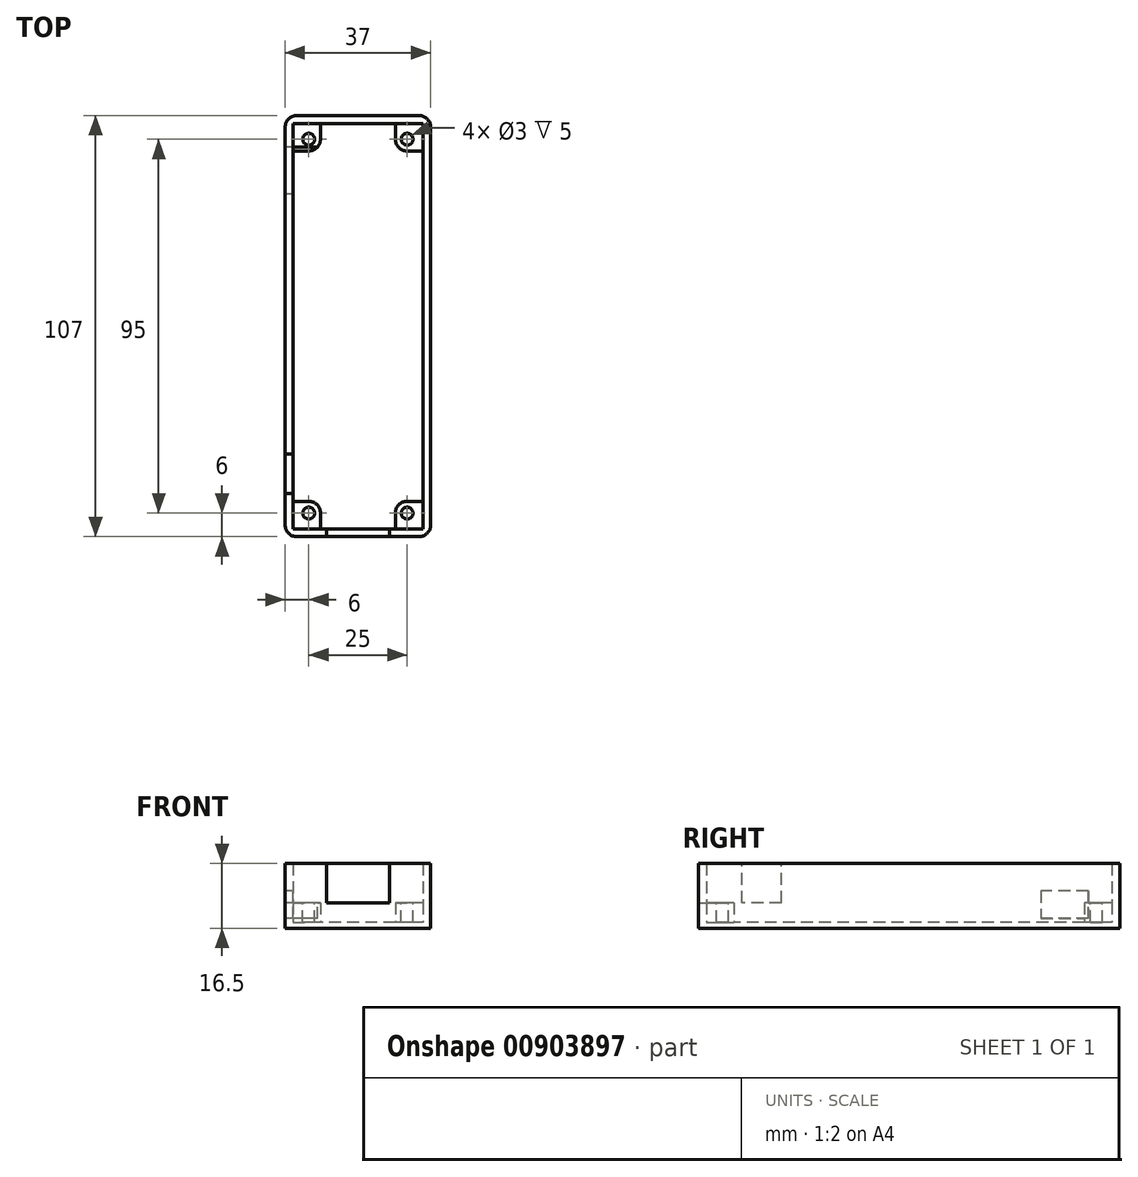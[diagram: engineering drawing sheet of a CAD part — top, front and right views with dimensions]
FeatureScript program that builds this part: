
annotation { "Feature Type Name" : "Feature", "Feature Type Description" : "" }
export const myFeature = defineFeature(function(context is Context, id is Id, definition is map)
    precondition{}
    {
        {
            var Q0;
            Q0=qCreatedBy(makeId("Top.planeOp"),FACE);
            var sketch = newSketch(context, id + "F0", { "sketchPlane" : qUnion([Q0])});
            skLineSegment(sketch, "E0.bottom", {"start": v(18.5, 53.5) * mm, "end": v(-18.5, 53.5) * mm});
            skLineSegment(sketch, "E0.top", {"start": v(18.5, -53.5) * mm, "end": v(-18.5, -53.5) * mm});
            skLineSegment(sketch, "E0.left", {"start": v(18.5, 53.5) * mm, "end": v(18.5, -53.5) * mm});
            skLineSegment(sketch, "E0.right", {"start": v(-18.5, 53.5) * mm, "end": v(-18.5, -53.5) * mm});
            skPoint(sketch, "E0.middle", {"position": v(0, 0) * mm});
            skSolve(sketch);
        }
        {
            var Q0;
            Q0=makeQuery(id+"F0.imprint","IMPRINT",FACE,{"disambiguationData":[TD([[makeQuery(id+"F0.imprint","IMPRINT",EDGE,{"derivedFrom":sQuery(id+"F0.wireOp",EDGE,"E0.bottom")}),1.0]])]});
            extrude(context, id + "F1", {"entities" : qUnion([Q0]), "depth" : 1.5 * mm, "offsetDistance" : 25 * mm});
        }
        {
            var Q0;
            Q0=makeQuery(id+"F1.opExtrude","CAP_FACE",FACE,{"disambiguationData":[OSD([sQuery(id+"F0.wireOp",EDGE,"E0.bottom"),sQuery(id+"F0.wireOp",EDGE,"E0.top"),sQuery(id+"F0.wireOp",EDGE,"E0.left"),sQuery(id+"F0.wireOp",EDGE,"E0.right")])],"isStart":false});
            var sketch = newSketch(context, id + "F2", { "sketchPlane" : qUnion([Q0])});
            skLineSegment(sketch, "E1.bottom", {"start": v(16.5, 51.5) * mm, "end": v(-16.5, 51.5) * mm});
            skLineSegment(sketch, "E1.top", {"start": v(16.5, -51.5) * mm, "end": v(-16.5, -51.5) * mm});
            skLineSegment(sketch, "E1.left", {"start": v(16.5, 51.5) * mm, "end": v(16.5, -51.5) * mm});
            skLineSegment(sketch, "E1.right", {"start": v(-16.5, 51.5) * mm, "end": v(-16.5, -51.5) * mm});
            skPoint(sketch, "E1.middle", {"position": v(0, 0) * mm});
            skSolve(sketch);
        }
        {
            var Q0;
            Q0=makeQuery(id+"F2.imprint","IMPRINT",FACE,{"disambiguationData":[TD([[makeQuery(id+"F2.imprint","IMPRINT",EDGE,{"derivedFrom":sQuery(id+"F2.wireOp",EDGE,"E1.bottom")}),-1.0]])]});
            extrude(context, id + "F3", {"entities" : qUnion([Q0]), "operationType" : NewBodyOperationType.ADD, "depth" : 15 * mm, "offsetDistance" : 25 * mm});
        }
        {
            var Q0;
            Q0=makeQuery(id+"F1.opExtrude","CAP_FACE",FACE,{"disambiguationData":[OSD([sQuery(id+"F0.wireOp",EDGE,"E0.bottom"),sQuery(id+"F0.wireOp",EDGE,"E0.top"),sQuery(id+"F0.wireOp",EDGE,"E0.left"),sQuery(id+"F0.wireOp",EDGE,"E0.right")])],"isStart":false});
            var sketch = newSketch(context, id + "F4", { "sketchPlane" : qUnion([Q0])});
            skLineSegment(sketch, "E2.bottom", {"start": v(-16.5, 51.5) * mm, "end": v(-9.5, 51.5) * mm});
            skLineSegment(sketch, "E2.top", {"start": v(-16.5, 44.5) * mm, "end": v(-9.5, 44.5) * mm});
            skLineSegment(sketch, "E2.left", {"start": v(-16.5, 51.5) * mm, "end": v(-16.5, 44.5) * mm});
            skLineSegment(sketch, "E2.right", {"start": v(-9.5, 51.5) * mm, "end": v(-9.5, 44.5) * mm});
            skLineSegment(sketch, "E3.MirrorCS", {"start": v(16.5, 51.5) * mm, "end": v(9.5, 51.5) * mm});
            skLineSegment(sketch, "E4.MirrorCS", {"start": v(9.5, 51.5) * mm, "end": v(9.5, 44.5) * mm});
            skLineSegment(sketch, "E5.MirrorCS", {"start": v(16.5, 44.5) * mm, "end": v(9.5, 44.5) * mm});
            skLineSegment(sketch, "E6.MirrorCS", {"start": v(16.5, 51.5) * mm, "end": v(16.5, 44.5) * mm});
            skLineSegment(sketch, "E7.MirrorCS", {"start": v(16.5, -44.5) * mm, "end": v(9.5, -44.5) * mm});
            skLineSegment(sketch, "E8.MirrorCS", {"start": v(-9.5, -51.5) * mm, "end": v(-9.5, -44.5) * mm});
            skLineSegment(sketch, "E9.MirrorCS", {"start": v(-16.5, -51.5) * mm, "end": v(-9.5, -51.5) * mm});
            skLineSegment(sketch, "E10.MirrorCS", {"start": v(16.5, -51.5) * mm, "end": v(16.5, -44.5) * mm});
            skLineSegment(sketch, "E11.MirrorCS", {"start": v(-16.5, -44.5) * mm, "end": v(-9.5, -44.5) * mm});
            skLineSegment(sketch, "E12.MirrorCS", {"start": v(-16.5, -51.5) * mm, "end": v(-16.5, -44.5) * mm});
            skLineSegment(sketch, "E13.MirrorCS", {"start": v(9.5, -51.5) * mm, "end": v(9.5, -44.5) * mm});
            skLineSegment(sketch, "E14.MirrorCS", {"start": v(16.5, -51.5) * mm, "end": v(9.5, -51.5) * mm});
            skSolve(sketch);
        }
        {
            var Q0;
            Q0 = qSketchRegion(id + "F4", true);
            extrude(context, id + "F5", {"entities" : qUnion([Q0]), "operationType" : NewBodyOperationType.ADD, "depth" : 5 * mm, "offsetDistance" : 25 * mm});
        }
        {
            var Q0;
            Q0=makeQuery(id+"F5.opExtrude","CAP_FACE",FACE,{"disambiguationData":[OSD([sQuery(id+"F4.wireOp",EDGE,"E2.bottom"),sQuery(id+"F4.wireOp",EDGE,"E2.top"),sQuery(id+"F4.wireOp",EDGE,"E2.left"),sQuery(id+"F4.wireOp",EDGE,"E2.right")])],"isStart":false});
            var sketch = newSketch(context, id + "F6", { "sketchPlane" : qUnion([Q0])});
            skLineSegment(sketch, "E15.bottom", {"start": v(12.5, 47.5) * mm, "end": v(-12.5, 47.5) * mm, "construction": true});
            skLineSegment(sketch, "E15.top", {"start": v(12.5, -47.5) * mm, "end": v(-12.5, -47.5) * mm, "construction": true});
            skLineSegment(sketch, "E15.left", {"start": v(12.5, 47.5) * mm, "end": v(12.5, -47.5) * mm, "construction": true});
            skLineSegment(sketch, "E15.right", {"start": v(-12.5, 47.5) * mm, "end": v(-12.5, -47.5) * mm, "construction": true});
            skPoint(sketch, "E15.middle", {"position": v(0, 0) * mm});
            skCircle(sketch, "E16", {"center": v(-12.5, 47.5) * mm, "radius": 1.5 * mm});
            skCircle(sketch, "E17.MirrorC", {"center": v(12.5, 47.5) * mm, "radius": 1.5 * mm});
            skLineSegment(sketch, "E18.MirrorCS", {"start": v(-12.5, 47.5) * mm, "end": v(12.5, 47.5) * mm, "construction": true});
            skLineSegment(sketch, "E19.MirrorCS", {"start": v(-12.5, -47.5) * mm, "end": v(12.5, -47.5) * mm, "construction": true});
            skCircle(sketch, "E20.MirrorC", {"center": v(12.5, -47.5) * mm, "radius": 1.5 * mm});
            skCircle(sketch, "E21.MirrorC", {"center": v(-12.5, -47.5) * mm, "radius": 1.5 * mm});
            skSolve(sketch);
        }
        {
            var Q0;
            Q0 = qSketchRegion(id + "F6", true);
            extrude(context, id + "F7", {"entities" : qUnion([Q0]), "operationType" : NewBodyOperationType.REMOVE, "oppositeDirection" : true, "depth" : 5 * mm, "offsetDistance" : 25 * mm});
        }
        {
            var Q0;
            Q0=makeQuery(id+"F5.opExtrude","SWEPT_EDGE",EDGE,{"disambiguationData":[OSD([sQuery(id+"F4.wireOp",EDGE,"E2.top"),sQuery(id+"F4.wireOp",EDGE,"E2.right")])]});
            var Q1;
            Q1=makeQuery(id+"F5.opExtrude","SWEPT_EDGE",EDGE,{"disambiguationData":[OSD([sQuery(id+"F4.wireOp",EDGE,"E4.MirrorCS"),sQuery(id+"F4.wireOp",EDGE,"E5.MirrorCS")])]});
            var Q2;
            Q2=makeQuery(id+"F5.opExtrude","SWEPT_EDGE",EDGE,{"disambiguationData":[OSD([sQuery(id+"F4.wireOp",EDGE,"E8.MirrorCS"),sQuery(id+"F4.wireOp",EDGE,"E11.MirrorCS")])]});
            var Q3;
            Q3=makeQuery(id+"F5.opExtrude","SWEPT_EDGE",EDGE,{"disambiguationData":[OSD([sQuery(id+"F4.wireOp",EDGE,"E7.MirrorCS"),sQuery(id+"F4.wireOp",EDGE,"E13.MirrorCS")])]});
            fillet(context, id + "F8", {"entities" : qUnion([Q0, Q1, Q2, Q3]), "radius" : 3 * mm, "tangentPropagation" : true, "allowEdgeOverflow" : false});
        }
        {
            var Q0;
            Q0=makeQuery(id+"F3.opExtrude","SWEPT_FACE",FACE,{"disambiguationData":[OSD([sQuery(id+"F2.wireOp",EDGE,"E1.top")])]});
            var sketch = newSketch(context, id + "F9", { "sketchPlane" : qUnion([Q0])});
            skLineSegment(sketch, "E22.bottom", {"start": v(0, 6.5) * mm, "end": v(8, 6.5) * mm});
            skLineSegment(sketch, "E22.top", {"start": v(0, 17.96) * mm, "end": v(8, 17.96) * mm});
            skLineSegment(sketch, "E22.left", {"start": v(0, 6.5) * mm, "end": v(0, 17.96) * mm});
            skLineSegment(sketch, "E22.right", {"start": v(8, 6.5) * mm, "end": v(8, 17.96) * mm});
            skLineSegment(sketch, "E23.MirrorCS", {"start": v(-8, 6.5) * mm, "end": v(-8, 17.96) * mm});
            skLineSegment(sketch, "E24.MirrorCS", {"start": v(0, 6.5) * mm, "end": v(-8, 6.5) * mm});
            skLineSegment(sketch, "E25.MirrorCS", {"start": v(0, 17.96) * mm, "end": v(-8, 17.96) * mm});
            skSolve(sketch);
        }
        {
            var Q0;
            Q0 = qSketchRegion(id + "F9", true);
            extrude(context, id + "F10", {"entities" : qUnion([Q0]), "operationType" : NewBodyOperationType.REMOVE, "oppositeDirection" : true, "depth" : 25 * mm, "offsetDistance" : 25 * mm});
        }
        {
            var Q0;
            {var subQ0=sQuery(id+"F0.wireOp",EDGE,"E0.right");Q0=makeQuery(id+"F3.boolean.opBoolean","MERGE",FACE,{"derivedFrom":[makeQuery(id+"F1.opExtrude","SWEPT_FACE",FACE,{"disambiguationData":[OSD([subQ0])]}),makeQuery(id+"F3.opExtrude","SWEPT_FACE",FACE,{"disambiguationData":[OSD([subQ0])]})]});}
            var sketch = newSketch(context, id + "F11", { "sketchPlane" : qUnion([Q0])});
            skLineSegment(sketch, "E26", {"start": v(-53.5, 6.5) * mm, "end": v(53.5, 6.5) * mm, "construction": true});
            skPoint(sketch, "E26.endSnap0", {"position": v(53.5, 8.25) * mm});
            skLineSegment(sketch, "E27.bottom", {"start": v(-45.5, 6.5) * mm, "end": v(-33.5, 6.5) * mm});
            skLineSegment(sketch, "E27.top", {"start": v(-45.5, 2.5) * mm, "end": v(-33.5, 2.5) * mm});
            skLineSegment(sketch, "E27.left", {"start": v(-45.5, 6.5) * mm, "end": v(-45.5, 2.5) * mm});
            skLineSegment(sketch, "E27.right", {"start": v(-33.5, 6.5) * mm, "end": v(-33.5, 2.5) * mm});
            skLineSegment(sketch, "E28.bottom", {"start": v(32.5, 6.5) * mm, "end": v(42.5, 6.5) * mm});
            skLineSegment(sketch, "E28.top", {"start": v(32.5, 19.27) * mm, "end": v(42.5, 19.27) * mm});
            skLineSegment(sketch, "E28.left", {"start": v(32.5, 6.5) * mm, "end": v(32.5, 19.27) * mm});
            skLineSegment(sketch, "E28.right", {"start": v(42.5, 6.5) * mm, "end": v(42.5, 19.27) * mm});
            skLineSegment(sketch, "E29", {"start": v(-47.5, 16.5) * mm, "end": v(-47.5, 0) * mm, "construction": true});
            skLineSegment(sketch, "E30", {"start": v(47.5, 16.5) * mm, "end": v(47.5, 0) * mm, "construction": true});
            skLineSegment(sketch, "E31.top", {"start": v(-45.5, 9.5) * mm, "end": v(-33.5, 9.5) * mm});
            skLineSegment(sketch, "E31.left", {"start": v(-45.5, 6.5) * mm, "end": v(-45.5, 9.5) * mm});
            skLineSegment(sketch, "E31.right", {"start": v(-33.5, 6.5) * mm, "end": v(-33.5, 9.5) * mm});
            skSolve(sketch);
        }
        {
            var Q0;
            Q0 = qSketchRegion(id + "F11", true);
            extrude(context, id + "F12", {"entities" : qUnion([Q0]), "operationType" : NewBodyOperationType.REMOVE, "oppositeDirection" : true, "depth" : 25 * mm, "offsetDistance" : 25 * mm});
        }
        {
            var Q0;
            {var subQ0=sQuery(id+"F0.wireOp",EDGE,"E0.left");var subQ1=sQuery(id+"F0.wireOp",EDGE,"E0.top");Q0=makeQuery(id+"F3.boolean.opBoolean","MERGE",EDGE,{"derivedFrom":[makeQuery(id+"F1.opExtrude","SWEPT_EDGE",EDGE,{"disambiguationData":[OSD([subQ1,subQ0])]}),makeQuery(id+"F3.opExtrude","SWEPT_EDGE",EDGE,{"disambiguationData":[OSD([subQ1,subQ0])]})]});}
            var Q1;
            {var subQ0=sQuery(id+"F0.wireOp",EDGE,"E0.right");var subQ1=sQuery(id+"F0.wireOp",EDGE,"E0.top");Q1=makeQuery(id+"F3.boolean.opBoolean","MERGE",EDGE,{"derivedFrom":[makeQuery(id+"F1.opExtrude","SWEPT_EDGE",EDGE,{"disambiguationData":[OSD([subQ1,subQ0])]}),makeQuery(id+"F3.opExtrude","SWEPT_EDGE",EDGE,{"disambiguationData":[OSD([subQ1,subQ0])]})]});}
            var Q2;
            {var subQ0=sQuery(id+"F0.wireOp",EDGE,"E0.right");var subQ1=sQuery(id+"F0.wireOp",EDGE,"E0.bottom");Q2=makeQuery(id+"F3.boolean.opBoolean","MERGE",EDGE,{"derivedFrom":[makeQuery(id+"F1.opExtrude","SWEPT_EDGE",EDGE,{"disambiguationData":[OSD([subQ1,subQ0])]}),makeQuery(id+"F3.opExtrude","SWEPT_EDGE",EDGE,{"disambiguationData":[OSD([subQ1,subQ0])]})]});}
            var Q3;
            {var subQ0=sQuery(id+"F0.wireOp",EDGE,"E0.left");var subQ1=sQuery(id+"F0.wireOp",EDGE,"E0.bottom");Q3=makeQuery(id+"F3.boolean.opBoolean","MERGE",EDGE,{"derivedFrom":[makeQuery(id+"F1.opExtrude","SWEPT_EDGE",EDGE,{"disambiguationData":[OSD([subQ1,subQ0])]}),makeQuery(id+"F3.opExtrude","SWEPT_EDGE",EDGE,{"disambiguationData":[OSD([subQ1,subQ0])]})]});}
            fillet(context, id + "F13", {"entities" : qUnion([Q0, Q1, Q2, Q3]), "radius" : 3 * mm, "tangentPropagation" : true, "allowEdgeOverflow" : false});
        }
    });
